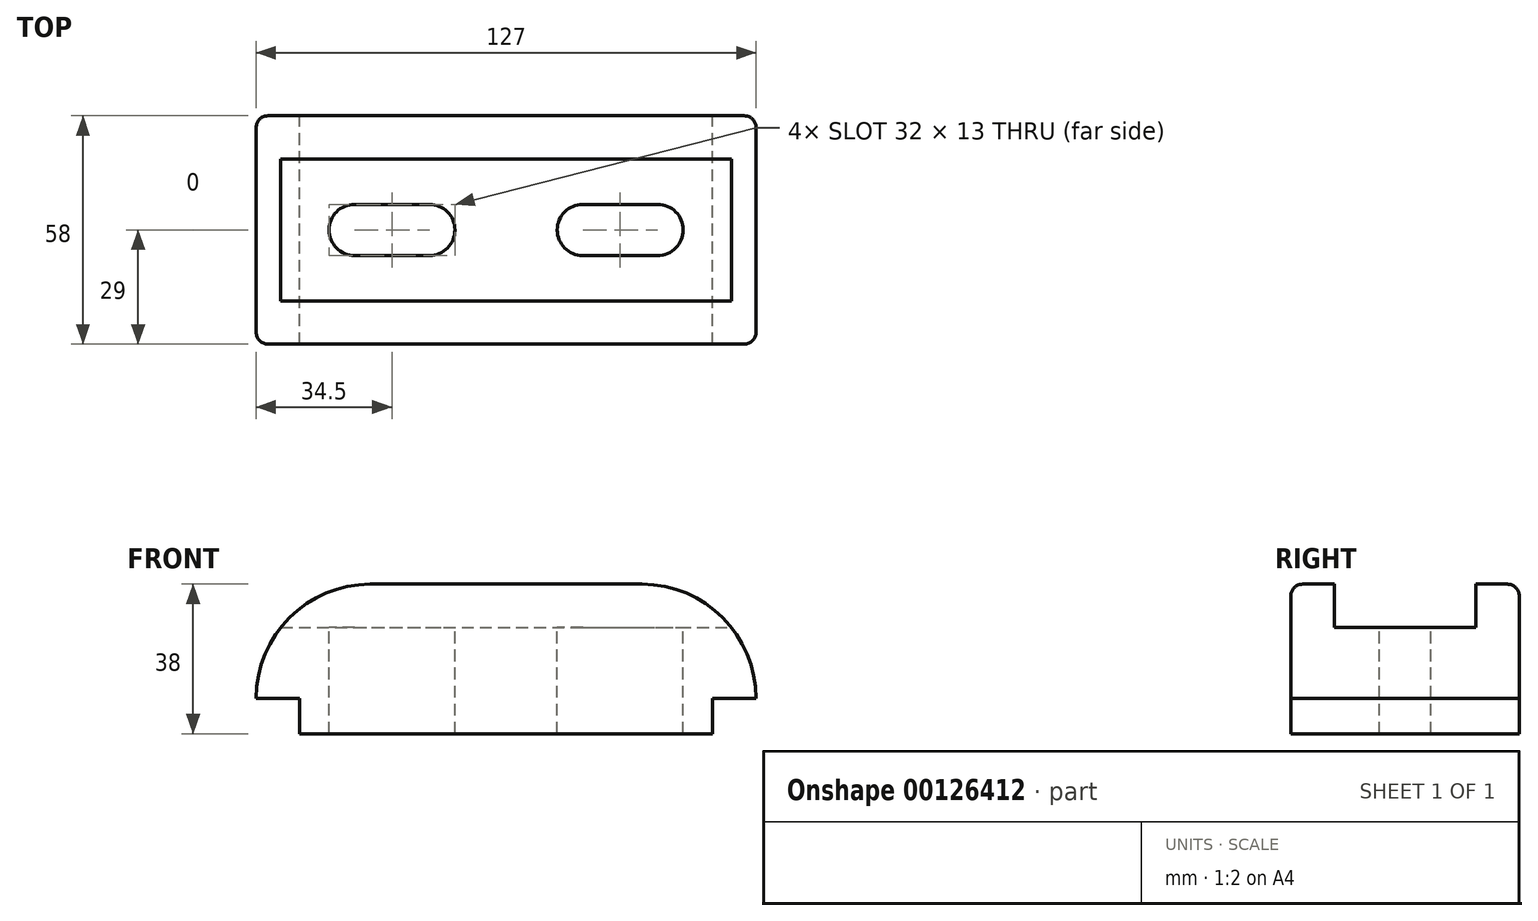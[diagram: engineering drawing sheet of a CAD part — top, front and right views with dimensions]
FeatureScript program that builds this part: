
annotation { "Feature Type Name" : "Feature", "Feature Type Description" : "" }
export const myFeature = defineFeature(function(context is Context, id is Id, definition is map)
    precondition{}
    {
        {
            var Q0;
            Q0=qCreatedBy(makeId("Front.planeOp"),FACE);
            var sketch = newSketch(context, id + "F0", { "sketchPlane" : qUnion([Q0])});
            skLineSegment(sketch, "E0", {"start": v(0, 0) * mm, "end": v(105, 0) * mm});
            skLineSegment(sketch, "E1", {"start": v(105, 0) * mm, "end": v(105, 9) * mm});
            skLineSegment(sketch, "E2", {"start": v(105, 9) * mm, "end": v(116, 9) * mm});
            skLineSegment(sketch, "E3", {"start": v(0, 0) * mm, "end": v(0, 9) * mm});
            skLineSegment(sketch, "E4", {"start": v(0, 9) * mm, "end": v(-11, 9) * mm});
            skLineSegment(sketch, "E5", {"start": v(18, 38) * mm, "end": v(87, 38) * mm});
            skArc(sketch, "E6", {"start": v(18, 38) * mm, "mid": v(-2.5, 29.5) * mm, "end": v(-11, 9) * mm});
            skArc(sketch, "E7", {"start": v(116, 9) * mm, "mid": v(107.5, 29.5) * mm, "end": v(87, 38) * mm});
            skLineSegment(sketch, "E8", {"start": v(54.53, 38) * mm, "end": v(54.53, 27) * mm, "construction": true});
            skLineSegment(sketch, "E9", {"start": v(54.53, 27) * mm, "end": v(-4.74, 27) * mm, "construction": true});
            skLineSegment(sketch, "E10", {"start": v(-4.74, 27) * mm, "end": v(109.74, 27) * mm});
            skSolve(sketch);
        }
        {
            var Q0;
            Q0=makeQuery(id+"F0.imprint","IMPRINT",FACE,{"disambiguationData":[TD([[makeQuery(id+"F0.imprint","IMPRINT",EDGE,{"derivedFrom":sQuery(id+"F0.wireOp",EDGE,"E0")}),1.0]])]});
            var Q1;
            {var subQ0=sQuery(id+"F0.wireOp",EDGE,"E5");Q1=makeQuery(id+"F0.imprint","IMPRINT",FACE,{"disambiguationData":[TD([[makeQuery(id+"F0.imprint","IMPRINT",EDGE,{"derivedFrom":subQ0}),-1.0]])]});}
            extrude(context, id + "F1", {"entities" : qUnion([Q0, Q1]), "endBound" : BoundingType.SYMMETRIC, "depth" : 58 * mm});
        }
        {
            var Q0;
            Q0=makeQuery(id+"F1.opExtrude","CAP_EDGE",EDGE,{"disambiguationData":[OSD([sQuery(id+"F0.wireOp",EDGE,"E5")])],"isStart":false});
            var Q1;
            Q1=makeQuery(id+"F1.opExtrude","CAP_EDGE",EDGE,{"disambiguationData":[OSD([sQuery(id+"F0.wireOp",EDGE,"E5")])],"isStart":true});
            fillet(context, id + "F2", {"entities" : qUnion([Q0, Q1]), "radius" : 3 * mm, "tangentPropagation" : true, "allowEdgeOverflow" : false});
        }
        {
            var Q0;
            {var subQ0=sQuery(id+"F0.wireOp",EDGE,"E5");Q0=makeQuery(id+"F0.imprint","IMPRINT",FACE,{"disambiguationData":[TD([[makeQuery(id+"F0.imprint","IMPRINT",EDGE,{"derivedFrom":subQ0}),-1.0]])]});}
            extrude(context, id + "F3", {"entities" : qUnion([Q0]), "operationType" : NewBodyOperationType.REMOVE, "endBound" : BoundingType.SYMMETRIC, "depth" : 36 * mm});
        }
        {
            var Q0;
            Q0=makeQuery(id+"F3.boolean.opBoolean","COPY",FACE,{"derivedFrom":makeQuery(id+"F3.opExtrude","SWEPT_FACE",FACE,{"disambiguationData":[OSD([sQuery(id+"F0.wireOp",EDGE,"E10")])]})});
            var sketch = newSketch(context, id + "F4", { "sketchPlane" : qUnion([Q0])});
            skLineSegment(sketch, "E11", {"start": v(0, 0) * mm, "end": v(106.8, 0) * mm, "construction": true});
            skLineSegment(sketch, "E12.0", {"start": v(0, -29) * mm, "end": v(0, 29) * mm});
            skLineSegment(sketch, "E13.0", {"start": v(105, -29) * mm, "end": v(105, 29) * mm});
            skLineSegment(sketch, "E14", {"start": v(14, -10.56) * mm, "end": v(14, 11.14) * mm, "construction": true});
            skLineSegment(sketch, "E15", {"start": v(33, -9.89) * mm, "end": v(33, 12.5) * mm, "construction": true});
            skLineSegment(sketch, "E16", {"start": v(72, -10.34) * mm, "end": v(72, 9.78) * mm, "construction": true});
            skLineSegment(sketch, "E17", {"start": v(91, -9.89) * mm, "end": v(91, 9.89) * mm, "construction": true});
            skCircle(sketch, "E18", {"center": v(14, 0) * mm, "radius": 6.5 * mm});
            skCircle(sketch, "E19", {"center": v(33, 0) * mm, "radius": 6.5 * mm});
            skArc(sketch, "E20", {"start": v(72, 6.5) * mm, "mid": v(65.5, 0) * mm, "end": v(72, -6.5) * mm});
            skCircle(sketch, "E21", {"center": v(91, 0) * mm, "radius": 6.5 * mm});
            skPoint(sketch, "E21.centerSnap0", {"position": v(91, 0) * mm});
            skLineSegment(sketch, "E22", {"start": v(14, 6.5) * mm, "end": v(33, 6.5) * mm});
            skLineSegment(sketch, "E23", {"start": v(14, -6.5) * mm, "end": v(33, -6.5) * mm});
            skLineSegment(sketch, "E24", {"start": v(72, 6.5) * mm, "end": v(91, 6.5) * mm});
            skLineSegment(sketch, "E25", {"start": v(72, -6.5) * mm, "end": v(91, -6.5) * mm});
            skSolve(sketch);
        }
        {
            var Q0;
            {var subQ0=sQuery(id+"F4.wireOp",EDGE,"E19");var subQ1=makeQuery(id+"F4.imprint","INTERSECT",VERTEX,{"derivedFrom":[subQ0,sQuery(id+"F4.wireOp",EDGE,"E22")]});Q0=makeQuery(id+"F4.imprint","IMPRINT",FACE,{"disambiguationData":[TD([[makeQuery(id+"F4.imprint","IMPRINT",EDGE,{"disambiguationData":[TD([[subQ1,-1.0]])],"derivedFrom":subQ0}),1.0]])]});}
            var Q1;
            Q1=makeQuery(id+"F4.imprint","IMPRINT",FACE,{"disambiguationData":[TD([[makeQuery(id+"F4.imprint","IMPRINT",EDGE,{"derivedFrom":sQuery(id+"F4.wireOp",EDGE,"E20")}),1.0]])]});
            var Q2;
            {var subQ0=sQuery(id+"F4.wireOp",EDGE,"E21");var subQ1=makeQuery(id+"F4.imprint","INTERSECT",VERTEX,{"derivedFrom":[subQ0,sQuery(id+"F4.wireOp",EDGE,"E24")]});Q2=makeQuery(id+"F4.imprint","IMPRINT",FACE,{"disambiguationData":[TD([[makeQuery(id+"F4.imprint","IMPRINT",EDGE,{"disambiguationData":[TD([[subQ1,-1.0]])],"derivedFrom":subQ0}),1.0]])]});}
            var Q3;
            {var subQ0=sQuery(id+"F4.wireOp",EDGE,"E22");Q3=makeQuery(id+"F4.imprint","IMPRINT",FACE,{"disambiguationData":[TD([[makeQuery(id+"F4.imprint","IMPRINT",EDGE,{"derivedFrom":subQ0}),-1.0]])]});}
            var Q4;
            {var subQ0=sQuery(id+"F4.wireOp",EDGE,"E18");var subQ1=makeQuery(id+"F4.imprint","INTERSECT",VERTEX,{"derivedFrom":[subQ0,sQuery(id+"F4.wireOp",EDGE,"E22")]});Q4=makeQuery(id+"F4.imprint","IMPRINT",FACE,{"disambiguationData":[TD([[makeQuery(id+"F4.imprint","IMPRINT",EDGE,{"disambiguationData":[TD([[subQ1,-1.0]])],"derivedFrom":subQ0}),1.0]])]});}
            extrude(context, id + "F5", {"entities" : qUnion([Q0, Q1, Q2, Q3, Q4]), "operationType" : NewBodyOperationType.REMOVE, "endBound" : BoundingType.THROUGH_ALL, "oppositeDirection" : true, "depth" : 25 * mm});
        }
    });
